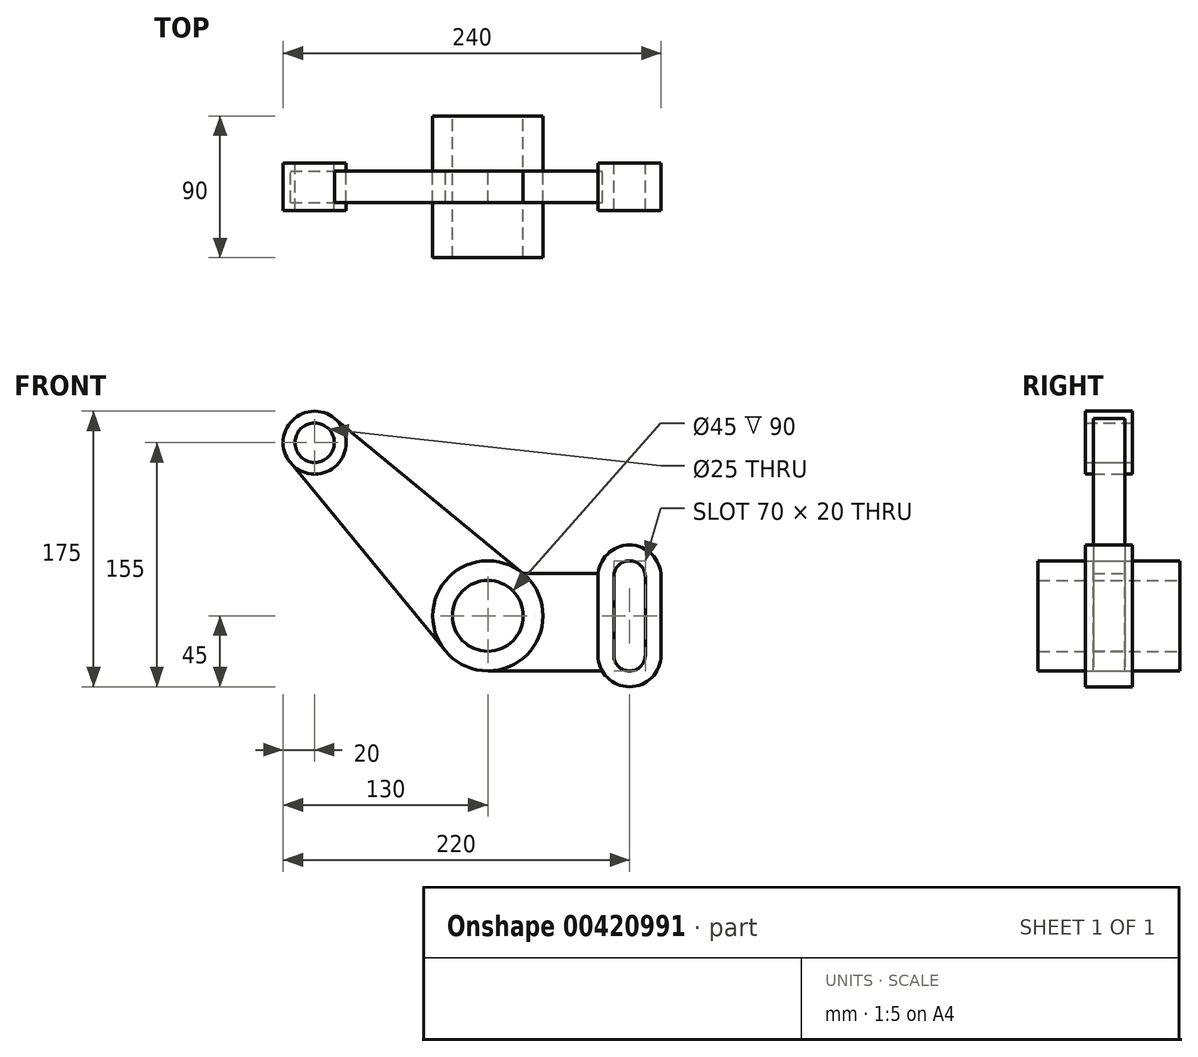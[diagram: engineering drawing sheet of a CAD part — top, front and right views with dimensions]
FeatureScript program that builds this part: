
annotation { "Feature Type Name" : "Feature", "Feature Type Description" : "" }
export const myFeature = defineFeature(function(context is Context, id is Id, definition is map)
    precondition{}
    {
        {
            var Q0;
            Q0=qCreatedBy(makeId("Front.planeOp"),FACE);
            var sketch = newSketch(context, id + "F0", { "sketchPlane" : qUnion([Q0])});
            skCircle(sketch, "E0", {"center": v(0, 0) * mm, "radius": 35 * mm});
            skCircle(sketch, "E1", {"center": v(0, 0) * mm, "radius": 22.5 * mm});
            skCircle(sketch, "E2", {"center": v(-110, 110) * mm, "radius": 20 * mm});
            skCircle(sketch, "E3", {"center": v(-110, 110) * mm, "radius": 12.5 * mm});
            skLineSegment(sketch, "E4", {"start": v(0, 0) * mm, "end": v(-122.88, 122.88) * mm, "construction": true});
            skLineSegment(sketch, "E5", {"start": v(0, 0) * mm, "end": v(-182.86, 0) * mm, "construction": true});
            skArc(sketch, "E6", {"start": v(100, 25) * mm, "mid": v(90, 35) * mm, "end": v(80, 25) * mm});
            skArc(sketch, "E7", {"start": v(110, 25) * mm, "mid": v(90, 45) * mm, "end": v(70, 25) * mm});
            skArc(sketch, "E8", {"start": v(80, -25) * mm, "mid": v(90, -35) * mm, "end": v(100, -25) * mm});
            skArc(sketch, "E9", {"start": v(70, -25) * mm, "mid": v(90, -45) * mm, "end": v(110, -25) * mm});
            skLineSegment(sketch, "E10", {"start": v(70, 25) * mm, "end": v(70, -25) * mm});
            skLineSegment(sketch, "E11", {"start": v(110, 25) * mm, "end": v(110, -25) * mm});
            skLineSegment(sketch, "E12", {"start": v(80, 25) * mm, "end": v(80, -25) * mm});
            skLineSegment(sketch, "E13", {"start": v(100, 25) * mm, "end": v(100, -25) * mm});
            skLineSegment(sketch, "E14", {"start": v(-97.29, 125.44) * mm, "end": v(22.25, 27.02) * mm});
            skLineSegment(sketch, "E15", {"start": v(-125.44, 97.29) * mm, "end": v(-27.02, -22.25) * mm});
            skLineSegment(sketch, "E16", {"start": v(0, -35) * mm, "end": v(72.68, -35) * mm});
            skLineSegment(sketch, "E17", {"start": v(22.25, 27.02) * mm, "end": v(70.1, 27.02) * mm});
            skLineSegment(sketch, "E18", {"start": v(0, 0) * mm, "end": v(90, 0) * mm, "construction": true});
            skLineSegment(sketch, "E19", {"start": v(90, 25) * mm, "end": v(90, -25) * mm, "construction": true});
            skSolve(sketch);
        }
        {
            var Q0;
            Q0=makeQuery(id+"F0.imprint","IMPRINT",FACE,{"disambiguationData":[TD([[makeQuery(id+"F0.imprint","IMPRINT",EDGE,{"derivedFrom":sQuery(id+"F0.wireOp",EDGE,"E3")}),-1.0]])]});
            var Q1;
            Q1=makeQuery(id+"F0.imprint","IMPRINT",FACE,{"disambiguationData":[TD([[makeQuery(id+"F0.imprint","IMPRINT",EDGE,{"derivedFrom":sQuery(id+"F0.wireOp",EDGE,"E6")}),-1.0]])]});
            extrude(context, id + "F1", {"entities" : qUnion([Q0, Q1]), "endBound" : BoundingType.SYMMETRIC, "depth" : 30 * mm});
        }
        {
            var Q0;
            Q0=makeQuery(id+"F0.imprint","IMPRINT",FACE,{"disambiguationData":[TD([[makeQuery(id+"F0.imprint","IMPRINT",EDGE,{"derivedFrom":sQuery(id+"F0.wireOp",EDGE,"E1")}),-1.0]])]});
            extrude(context, id + "F2", {"entities" : qUnion([Q0]), "endBound" : BoundingType.SYMMETRIC, "depth" : 90 * mm});
        }
        {
            var Q0;
            {var subQ0=sQuery(id+"F0.wireOp",EDGE,"E14");Q0=makeQuery(id+"F0.imprint","IMPRINT",FACE,{"disambiguationData":[TD([[makeQuery(id+"F0.imprint","IMPRINT",EDGE,{"derivedFrom":subQ0}),-1.0]])]});}
            var Q1;
            {var subQ0=sQuery(id+"F0.wireOp",EDGE,"E10");Q1=makeQuery(id+"F0.imprint","IMPRINT",FACE,{"disambiguationData":[TD([[makeQuery(id+"F0.imprint","IMPRINT",EDGE,{"derivedFrom":subQ0}),-1.0]])]});}
            extrude(context, id + "F3", {"entities" : qUnion([Q0, Q1]), "endBound" : BoundingType.SYMMETRIC, "depth" : 20 * mm});
        }
    });
